# Revit family: Polyurethane Buffer 2xBumper
name_source: partatom
category: Generic Models
units: mm (PartAtom-declared; Revit-internal decimal feet)

## family parameters
Always vertical = Yes
Can host rebar = No
Cut with Voids When Loaded = No
Part Type = Normal
Room Calculation Point = No
Round Connector Dimension = Use Diameter
Shared = No
Work Plane-Based = No

## types (1)
- Polyurethane Buffer 2xBumper
    Base Plate Length = 140 mm  [stored 0.459318 ft]
    Base Plate Thickness = 12 mm  [stored 0.0393701 ft]
    Base Plate With = 140 mm  [stored 0.459318 ft]
    Bumper Diameter = 115 mm  [stored 0.377297 ft]
    Bumper Height = 55 mm  [stored 0.180446 ft]
    Default Elevation = 0 mm  [stored 0 ft]
    Height to First Bumper = 67 mm
    LiftBufer_ImpactMassRange = 1500
    LiftBuffer_FixedToCar = Yes
    LiftBuffer_RatedSpeed = 1.0 m/s

note: [stored X ft] marks values corroborated as IEEE doubles in the binary element streams (Revit-internal decimal feet)

## geometry (parser evidence)
native form markers: Sweep x3
no freeform markers — native parametric forms only
